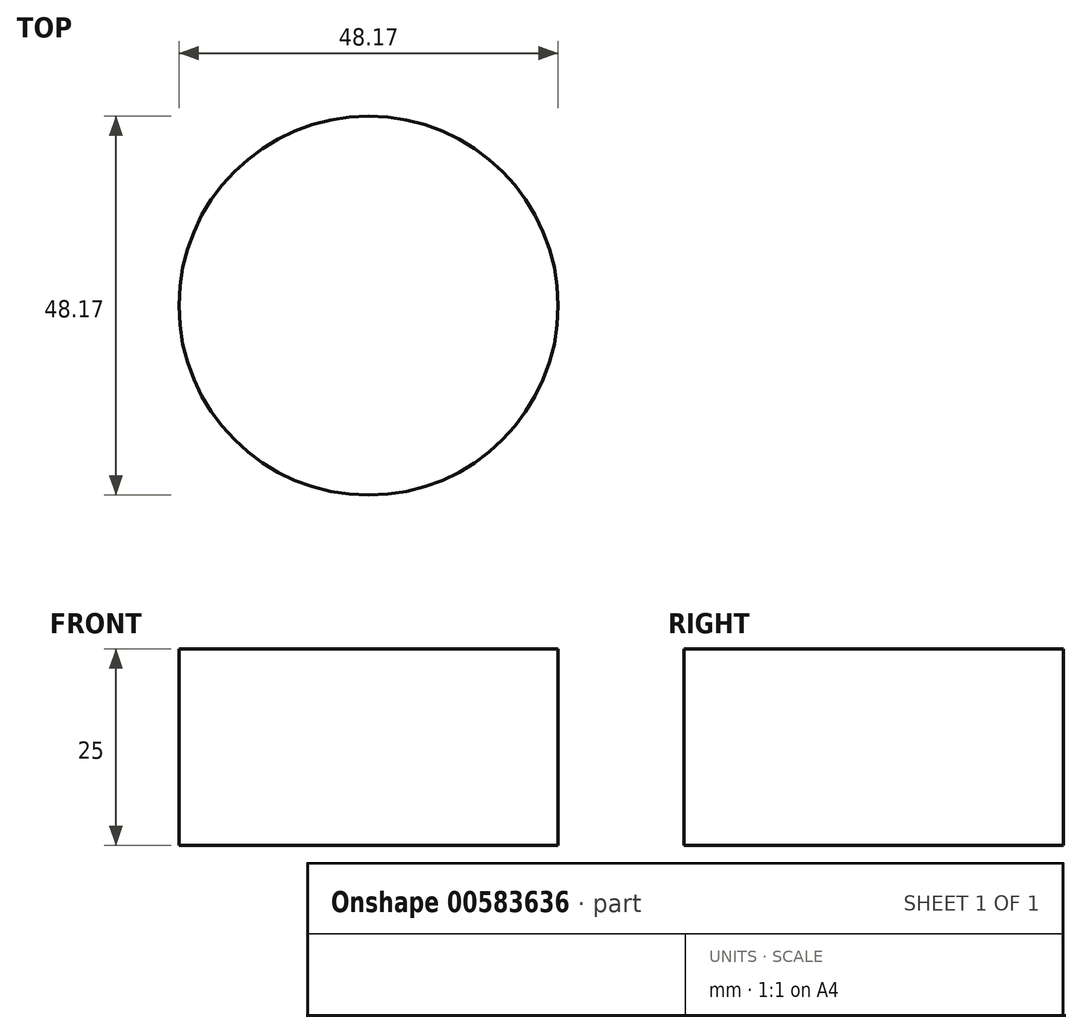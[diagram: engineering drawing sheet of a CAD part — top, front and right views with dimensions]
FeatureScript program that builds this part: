
annotation { "Feature Type Name" : "Feature", "Feature Type Description" : "" }
export const myFeature = defineFeature(function(context is Context, id is Id, definition is map)
    precondition{}
    {
        {
            var Q0;
            Q0=qCreatedBy(makeId("Top.planeOp"),FACE);
            var sketch = newSketch(context, id + "F0", { "sketchPlane" : qUnion([Q0])});
            skCircle(sketch, "E0", {"center": v(-70.85, -27.3) * mm, "radius": 24.08 * mm});
            skSolve(sketch);
        }
        {
            var Q0;
            Q0=makeQuery(id+"F0.imprint","IMPRINT",FACE,{"disambiguationData":[TD([[makeQuery(id+"F0.imprint","IMPRINT",EDGE,{"derivedFrom":sQuery(id+"F0.wireOp",EDGE,"E0")}),1.0]])]});
            extrude(context, id + "F1", {"entities" : qUnion([Q0]), "depth" : 25 * mm, "offsetDistance" : 25 * mm});
        }
    });
